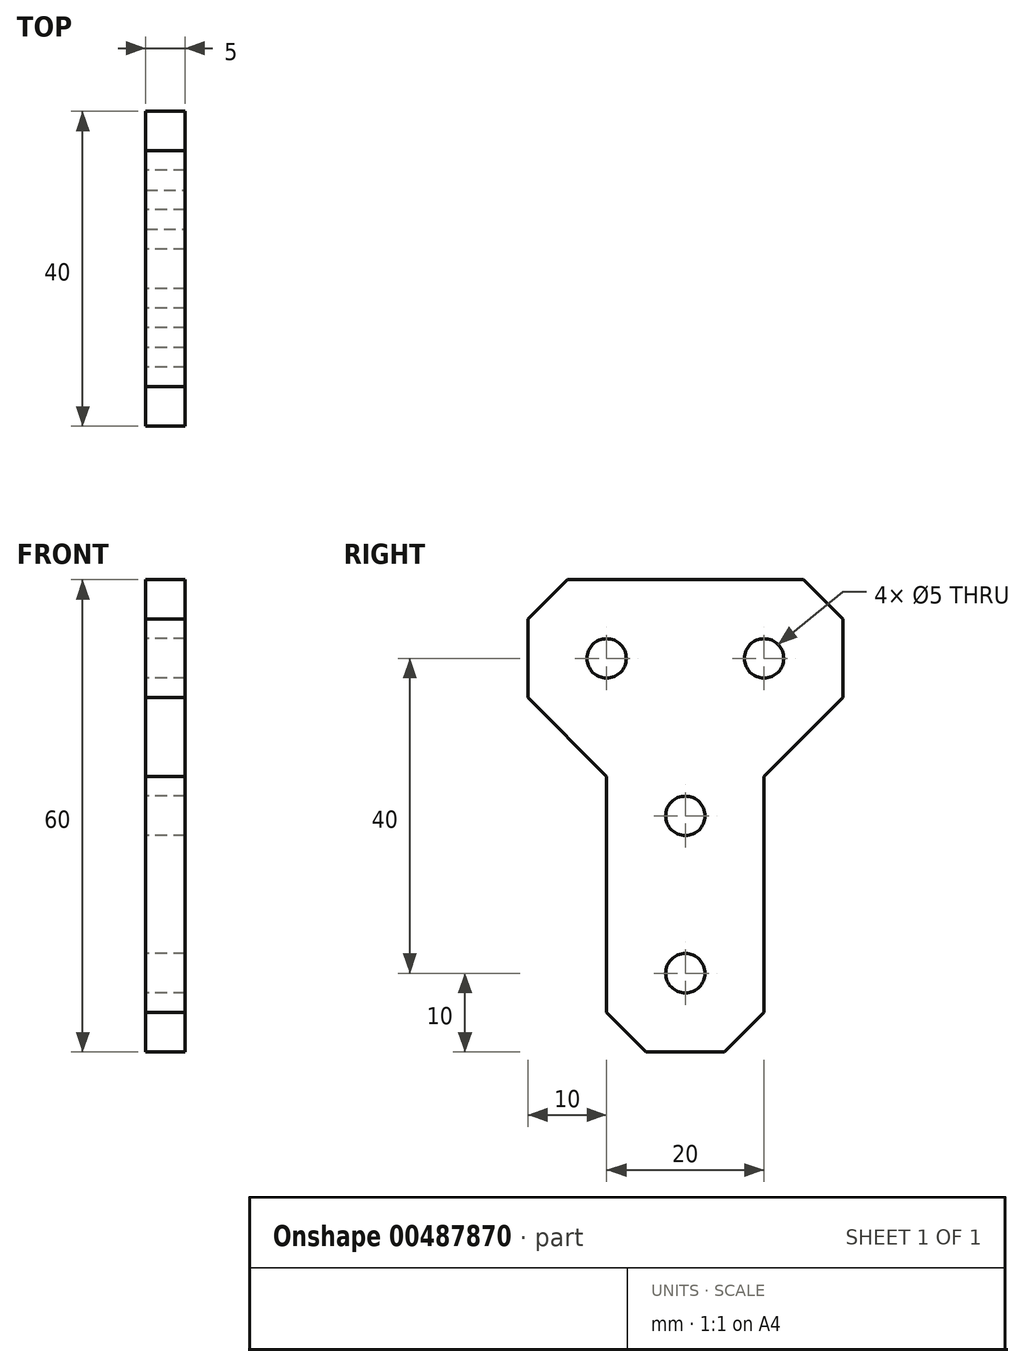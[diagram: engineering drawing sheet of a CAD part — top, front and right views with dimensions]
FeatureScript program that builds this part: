
annotation { "Feature Type Name" : "Feature", "Feature Type Description" : "" }
export const myFeature = defineFeature(function(context is Context, id is Id, definition is map)
    precondition{}
    {
        {
            var Q0;
            Q0=qCreatedBy(makeId("Right.planeOp"),FACE);
            var sketch = newSketch(context, id + "F0", { "sketchPlane" : qUnion([Q0])});
            skLineSegment(sketch, "E0.top", {"start": v(10, 0) * mm, "end": v(-10, 0) * mm});
            skLineSegment(sketch, "E0.left", {"start": v(10, 40) * mm, "end": v(10, 0) * mm});
            skLineSegment(sketch, "E0.right", {"start": v(-10, 40) * mm, "end": v(-10, 0) * mm});
            skPoint(sketch, "E0.middle", {"position": v(0, 20) * mm});
            skLineSegment(sketch, "E1.bottom", {"start": v(20, 40) * mm, "end": v(10, 40) * mm});
            skLineSegment(sketch, "E1.top", {"start": v(20, 60) * mm, "end": v(-20, 60) * mm});
            skLineSegment(sketch, "E1.left", {"start": v(20, 40) * mm, "end": v(20, 60) * mm});
            skLineSegment(sketch, "E1.right", {"start": v(-20, 40) * mm, "end": v(-20, 60) * mm});
            skPoint(sketch, "E1.middle", {"position": v(0, 50) * mm});
            skLineSegment(sketch, "E2.trimOffspring", {"start": v(-10, 40) * mm, "end": v(-20, 40) * mm});
            skCircle(sketch, "E3", {"center": v(-10, 50) * mm, "radius": 2.5 * mm});
            skCircle(sketch, "E4", {"center": v(10, 50) * mm, "radius": 2.5 * mm});
            skCircle(sketch, "E5", {"center": v(0, 30) * mm, "radius": 2.5 * mm});
            skCircle(sketch, "E6", {"center": v(0, 10) * mm, "radius": 2.5 * mm});
            skLineSegment(sketch, "E7", {"start": v(0, 0) * mm, "end": v(0, 20) * mm, "construction": true});
            skLineSegment(sketch, "E8", {"start": v(0, 20) * mm, "end": v(0, 40) * mm, "construction": true});
            skSolve(sketch);
        }
        {
            var Q0;
            Q0 = qSketchRegion(id + "F0", true);
            extrude(context, id + "F1", {"entities" : qUnion([Q0]), "depth" : 5 * mm, "offsetDistance" : 25 * mm});
        }
        {
            var Q0;
            Q0=makeQuery(id+"F1.opExtrude","SWEPT_EDGE",EDGE,{"disambiguationData":[OSD([sQuery(id+"F0.wireOp",EDGE,"E0.left"),sQuery(id+"F0.wireOp",EDGE,"E1.bottom")])]});
            var Q1;
            Q1=makeQuery(id+"F1.opExtrude","SWEPT_EDGE",EDGE,{"disambiguationData":[OSD([sQuery(id+"F0.wireOp",EDGE,"E1.bottom"),sQuery(id+"F0.wireOp",EDGE,"E1.left")])]});
            var Q2;
            Q2=makeQuery(id+"F1.opExtrude","SWEPT_EDGE",EDGE,{"disambiguationData":[OSD([sQuery(id+"F0.wireOp",EDGE,"E1.top"),sQuery(id+"F0.wireOp",EDGE,"E1.left")])]});
            var Q3;
            Q3=makeQuery(id+"F1.opExtrude","SWEPT_EDGE",EDGE,{"disambiguationData":[OSD([sQuery(id+"F0.wireOp",EDGE,"E0.top"),sQuery(id+"F0.wireOp",EDGE,"E0.left")])]});
            var Q4;
            Q4=makeQuery(id+"F1.opExtrude","SWEPT_EDGE",EDGE,{"disambiguationData":[OSD([sQuery(id+"F0.wireOp",EDGE,"E0.top"),sQuery(id+"F0.wireOp",EDGE,"E0.right")])]});
            var Q5;
            Q5=makeQuery(id+"F1.opExtrude","SWEPT_EDGE",EDGE,{"disambiguationData":[OSD([sQuery(id+"F0.wireOp",EDGE,"E0.right"),sQuery(id+"F0.wireOp",EDGE,"E2.trimOffspring")])]});
            var Q6;
            Q6=makeQuery(id+"F1.opExtrude","SWEPT_EDGE",EDGE,{"disambiguationData":[OSD([sQuery(id+"F0.wireOp",EDGE,"E1.right"),sQuery(id+"F0.wireOp",EDGE,"E2.trimOffspring")])]});
            var Q7;
            Q7=makeQuery(id+"F1.opExtrude","SWEPT_EDGE",EDGE,{"disambiguationData":[OSD([sQuery(id+"F0.wireOp",EDGE,"E1.top"),sQuery(id+"F0.wireOp",EDGE,"E1.right")])]});
            chamfer(context, id + "F2", {"entities" : qUnion([Q0, Q1, Q2, Q3, Q4, Q5, Q6, Q7]), "width" : 5 * mm, "tangentPropagation" : true});
        }
    });
